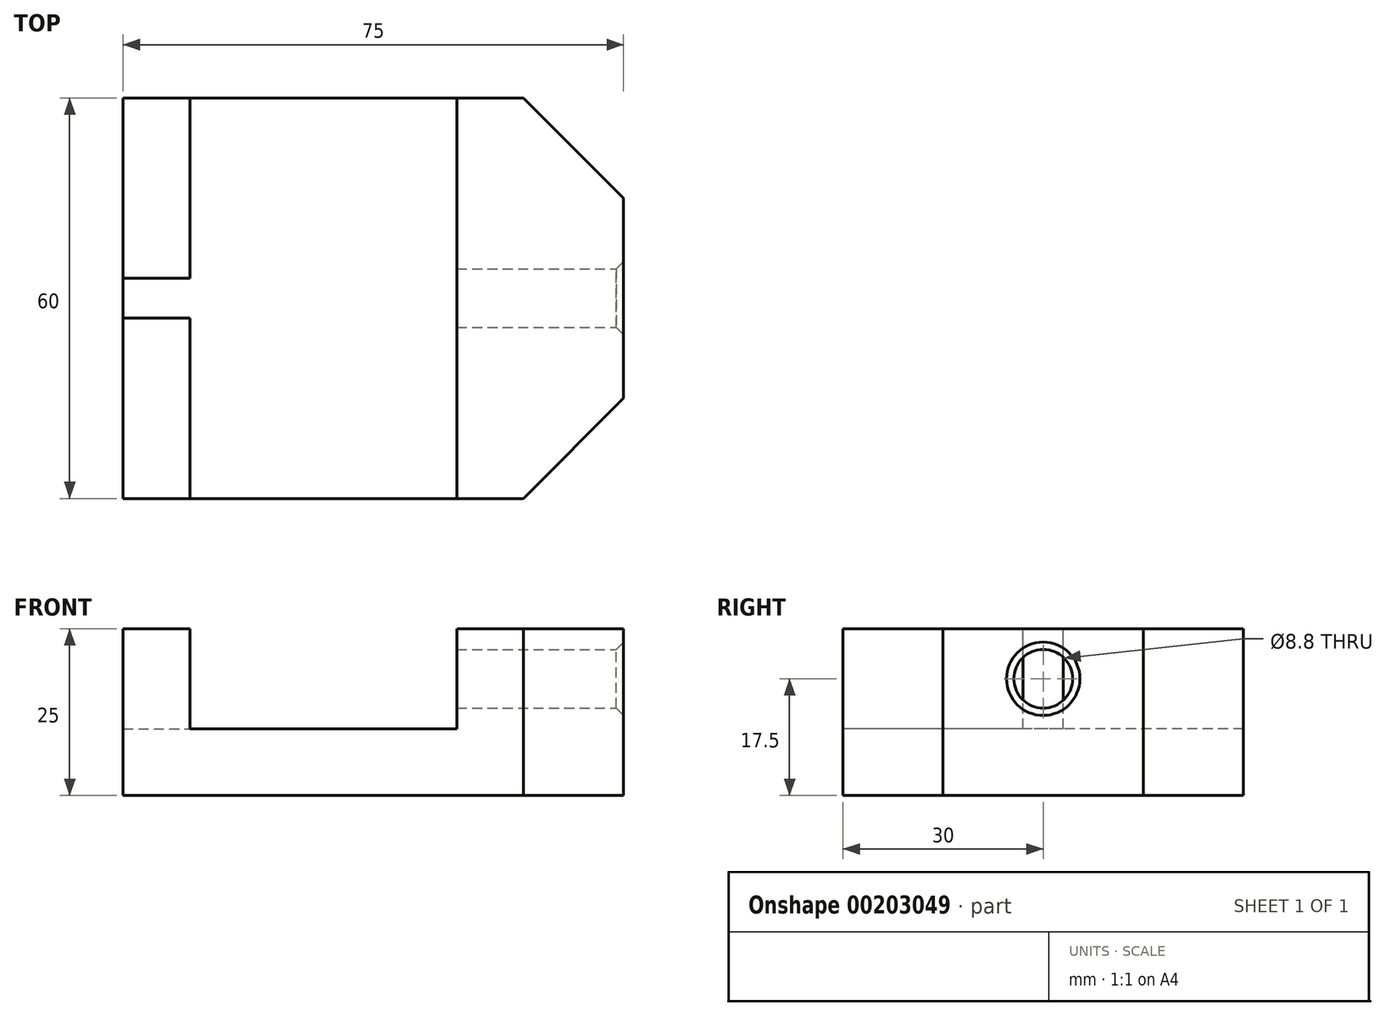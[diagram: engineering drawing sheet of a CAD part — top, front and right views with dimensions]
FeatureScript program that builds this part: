
annotation { "Feature Type Name" : "Feature", "Feature Type Description" : "" }
export const myFeature = defineFeature(function(context is Context, id is Id, definition is map)
    precondition{}
    {
        {
            var Q0;
            Q0=qCreatedBy(makeId("Top.planeOp"),FACE);
            var sketch = newSketch(context, id + "F7", { "sketchPlane" : qUnion([Q0])});
            skLineSegment(sketch, "E0.bottom", {"start": v(-50, 30) * mm, "end": v(10, 30) * mm});
            skLineSegment(sketch, "E0.top", {"start": v(-50, -30) * mm, "end": v(10, -30) * mm});
            skLineSegment(sketch, "E0.left", {"start": v(-50, 30) * mm, "end": v(-50, -30) * mm});
            skPoint(sketch, "E0.middle", {"position": v(0, 0) * mm});
            skLineSegment(sketch, "E1", {"start": v(-40, -30) * mm, "end": v(-40, 30) * mm});
            skLineSegment(sketch, "E2", {"start": v(0, -30) * mm, "end": v(0, 30) * mm});
            skLineSegment(sketch, "E3", {"start": v(10, -30) * mm, "end": v(25, -15) * mm});
            skLineSegment(sketch, "E4.MirrorCS", {"start": v(10, 30) * mm, "end": v(25, 15) * mm});
            skPoint(sketch, "E5.orphan", {"position": v(50, 30) * mm});
            skPoint(sketch, "E6.orphan", {"position": v(50, -30) * mm});
            skLineSegment(sketch, "E7", {"start": v(25, 15) * mm, "end": v(25, -15) * mm});
            skSolve(sketch);
        }
        {
            var Q0;
            {var subQ0=sQuery(id+"F7.wireOp",EDGE,"E0.left");Q0=makeQuery(id+"F7.imprint","IMPRINT",FACE,{"disambiguationData":[TD([[makeQuery(id+"F7.imprint","IMPRINT",EDGE,{"derivedFrom":subQ0}),1.0]])]});}
            var Q1;
            {var subQ3=sQuery(id+"F7.wireOp",EDGE,"E2");Q1=makeQuery(id+"F7.imprint","IMPRINT",FACE,{"disambiguationData":[TD([[makeQuery(id+"F7.imprint","IMPRINT",EDGE,{"derivedFrom":subQ3}),-1.0]])]});}
            var Q2;
            {var subQ0=sQuery(id+"F7.wireOp",EDGE,"E1");Q2=makeQuery(id+"F7.imprint","IMPRINT",FACE,{"disambiguationData":[TD([[makeQuery(id+"F7.imprint","IMPRINT",EDGE,{"derivedFrom":subQ0}),-1.0]])]});}
            extrude(context, id + "F0", {"entities" : qUnion([Q0, Q1, Q2]), "depth" : 10 * mm});
        }
        {
            var Q0;
            {var subQ0=sQuery(id+"F7.wireOp",EDGE,"E0.left");Q0=makeQuery(id+"F7.imprint","IMPRINT",FACE,{"disambiguationData":[TD([[makeQuery(id+"F7.imprint","IMPRINT",EDGE,{"derivedFrom":subQ0}),1.0]])]});}
            var Q1;
            {var subQ3=sQuery(id+"F7.wireOp",EDGE,"E2");Q1=makeQuery(id+"F7.imprint","IMPRINT",FACE,{"disambiguationData":[TD([[makeQuery(id+"F7.imprint","IMPRINT",EDGE,{"derivedFrom":subQ3}),-1.0]])]});}
            extrude(context, id + "F1", {"entities" : qUnion([Q0, Q1]), "operationType" : NewBodyOperationType.ADD, "depth" : 25 * mm});
        }
        {
            var Q0;
            Q0=makeQuery(id+"F1.opExtrude","CAP_FACE",FACE,{"disambiguationData":[OSD([sQuery(id+"F7.wireOp",EDGE,"E0.bottom"),sQuery(id+"F7.wireOp",EDGE,"E0.top"),sQuery(id+"F7.wireOp",EDGE,"E0.left"),sQuery(id+"F7.wireOp",EDGE,"E1")])],"isStart":false});
            var sketch = newSketch(context, id + "F2", { "sketchPlane" : qUnion([Q0])});
            skLineSegment(sketch, "E8.bottom", {"start": v(-50, 3) * mm, "end": v(-40, 3) * mm});
            skLineSegment(sketch, "E8.top", {"start": v(-50, -3) * mm, "end": v(-40, -3) * mm});
            skLineSegment(sketch, "E8.left", {"start": v(-50, 3) * mm, "end": v(-50, -3) * mm});
            skLineSegment(sketch, "E8.right", {"start": v(-40, 3) * mm, "end": v(-40, -3) * mm});
            skPoint(sketch, "E8.middle", {"position": v(-45, 0) * mm});
            skPoint(sketch, "E8.middle.positionSnap0", {"position": v(-50, 0) * mm});
            skPoint(sketch, "E8.centerSnap0", {"position": v(-50, 0) * mm});
            skSolve(sketch);
        }
        {
            var Q0;
            Q0=makeQuery(id+"F2.imprint","IMPRINT",FACE,{"disambiguationData":[TD([[makeQuery(id+"F2.imprint","IMPRINT",EDGE,{"derivedFrom":sQuery(id+"F2.wireOp",EDGE,"E8.bottom")}),-1.0]])]});
            extrude(context, id + "F3", {"entities" : qUnion([Q0]), "operationType" : NewBodyOperationType.REMOVE, "oppositeDirection" : true, "depth" : 15 * mm});
        }
        {
            var Q0;
            Q0=makeQuery(id+"F1.opExtrude","SWEPT_FACE",FACE,{"disambiguationData":[OSD([sQuery(id+"F7.wireOp",EDGE,"E2")])]});
            var sketch = newSketch(context, id + "F4", { "sketchPlane" : qUnion([Q0])});
            skPoint(sketch, "E9", {"position": v(0, 17.5) * mm});
            skSolve(sketch);
        }
        {
            var Q0;
            {var subQ0=sQuery(id+"F7.wireOp",EDGE,"E7");Q0=makeQuery(id+"F1.boolean.opBoolean","MERGE",FACE,{"derivedFrom":[makeQuery(id+"F0.opExtrude","SWEPT_FACE",FACE,{"disambiguationData":[OSD([subQ0])]}),makeQuery(id+"F1.opExtrude","SWEPT_FACE",FACE,{"disambiguationData":[OSD([subQ0])]})]});}
            var sketch = newSketch(context, id + "F5", { "sketchPlane" : qUnion([Q0])});
            skPoint(sketch, "E10", {"position": v(0, 17.5) * mm});
            skSolve(sketch);
        }
        {
            var Q0;
            Q0=sQuery(id+"F5.wireOp",VERTEX,"E10");
            var Q1;
            Q1=makeQuery(id+"F0.opExtrude","SWEPT_BODY",BODY,{"disambiguationData":[OSD([sQuery(id+"F7.wireOp",EDGE,"E0.bottom"),sQuery(id+"F7.wireOp",EDGE,"E0.top"),sQuery(id+"F7.wireOp",EDGE,"E0.left"),sQuery(id+"F7.wireOp",EDGE,"E3"),sQuery(id+"F7.wireOp",EDGE,"E4.MirrorCS"),sQuery(id+"F7.wireOp",EDGE,"E7")])]});
            hole(context, id + "F6", {"style" : HoleStyle.C_SINK, "endStyle" : HoleEndStyle.BLIND, "holeDiameter" : 8.8 * mm, "cSinkDiameter" : 11 * mm, "cSinkAngle" : 90 * degree, "holeDepth" : 25 * mm, "startFromSketch" : true, "locations" : qUnion([Q0]), "scope" : qUnion([Q1])});
        }
    });
